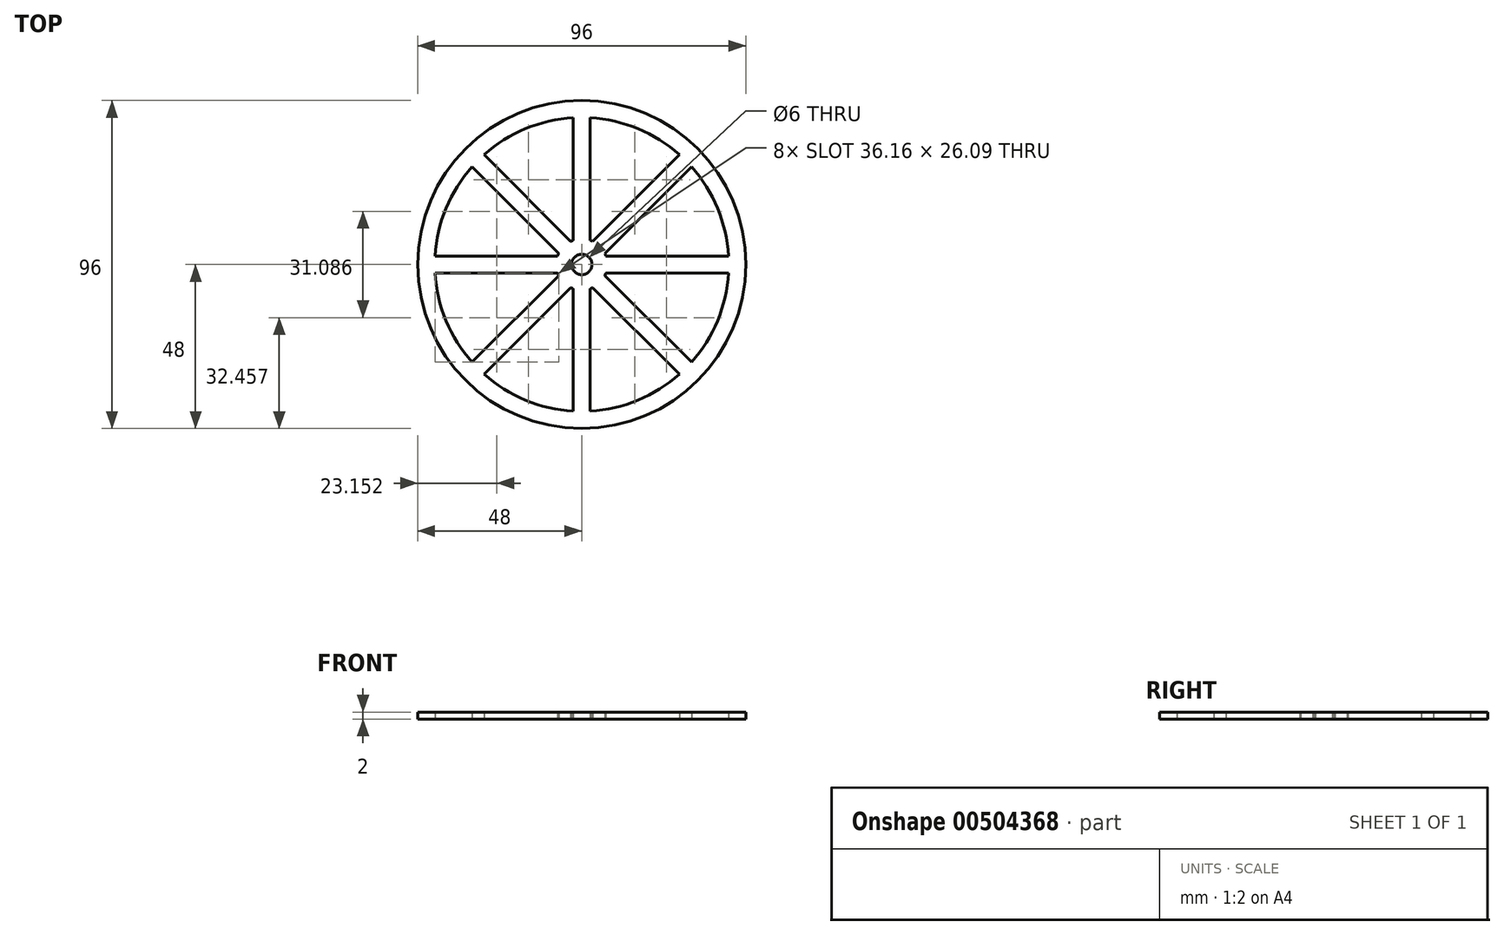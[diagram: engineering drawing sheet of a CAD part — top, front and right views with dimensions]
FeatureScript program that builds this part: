
annotation { "Feature Type Name" : "Feature", "Feature Type Description" : "" }
export const myFeature = defineFeature(function(context is Context, id is Id, definition is map)
    precondition{}
    {
        {
            var Q0;
            Q0=qCreatedBy(makeId("Top.planeOp"),FACE);
            var sketch = newSketch(context, id + "F0", { "sketchPlane" : qUnion([Q0])});
            skArc(sketch, "E0", {"start": v(-32.12, 28.59) * mm, "mid": v(-39.73, 16.46) * mm, "end": v(-42.93, 2.5) * mm});
            skCircle(sketch, "E1", {"center": v(0, 0) * mm, "radius": 48 * mm});
            skLineSegment(sketch, "E2", {"start": v(0, 0) * mm, "end": v(-28.59, 28.59) * mm, "construction": true});
            skLineSegment(sketch, "E3.left", {"start": v(-2.5, 42.93) * mm, "end": v(-2.5, 7.07) * mm});
            skLineSegment(sketch, "E3.right", {"start": v(2.5, 42.93) * mm, "end": v(2.5, 7.07) * mm});
            skLineSegment(sketch, "E4.bottom", {"start": v(-42.93, 2.5) * mm, "end": v(-7.07, 2.5) * mm});
            skLineSegment(sketch, "E4.top", {"start": v(-42.93, -2.5) * mm, "end": v(-7.07, -2.5) * mm});
            skLineSegment(sketch, "E5", {"start": v(-28.59, 32.12) * mm, "end": v(-3.23, 6.77) * mm});
            skLineSegment(sketch, "E6.MirrorCS", {"start": v(-32.12, 28.59) * mm, "end": v(-6.77, 3.23) * mm});
            skLineSegment(sketch, "E7.MirrorCS", {"start": v(28.59, 32.12) * mm, "end": v(3.23, 6.77) * mm});
            skArc(sketch, "E8", {"start": v(-2.5, 7.07) * mm, "mid": v(-2.87, 6.93) * mm, "end": v(-3.23, 6.77) * mm});
            skArc(sketch, "E9.trimOffspring", {"start": v(-6.77, 3.23) * mm, "mid": v(-6.93, 2.87) * mm, "end": v(-7.07, 2.5) * mm});
            skArc(sketch, "E10.trimOffspring", {"start": v(-7.07, -2.5) * mm, "mid": v(-6.93, -2.87) * mm, "end": v(-6.77, -3.23) * mm});
            skLineSegment(sketch, "E11.trimOffspring", {"start": v(-6.77, -3.23) * mm, "end": v(-32.12, -28.59) * mm});
            skArc(sketch, "E12.trimOffspring", {"start": v(-3.23, -6.77) * mm, "mid": v(-2.87, -6.93) * mm, "end": v(-2.5, -7.07) * mm});
            skLineSegment(sketch, "E13.trimOffspring", {"start": v(-3.23, -6.77) * mm, "end": v(-28.59, -32.12) * mm});
            skLineSegment(sketch, "E14.trimOffspring", {"start": v(-2.5, -7.07) * mm, "end": v(-2.5, -42.93) * mm});
            skLineSegment(sketch, "E15.trimOffspring", {"start": v(2.5, -7.07) * mm, "end": v(2.5, -42.93) * mm});
            skLineSegment(sketch, "E16.trimOffspring", {"start": v(3.23, -6.77) * mm, "end": v(28.59, -32.12) * mm});
            skArc(sketch, "E17.trimOffspring", {"start": v(2.5, -7.07) * mm, "mid": v(2.87, -6.93) * mm, "end": v(3.23, -6.77) * mm});
            skArc(sketch, "E18.trimOffspring", {"start": v(6.77, -3.23) * mm, "mid": v(6.93, -2.87) * mm, "end": v(7.07, -2.5) * mm});
            skLineSegment(sketch, "E19.trimOffspring", {"start": v(6.77, -3.23) * mm, "end": v(32.12, -28.59) * mm});
            skLineSegment(sketch, "E20.trimOffspring", {"start": v(7.07, -2.5) * mm, "end": v(42.93, -2.5) * mm});
            skArc(sketch, "E21.trimOffspring", {"start": v(7.07, 2.5) * mm, "mid": v(6.93, 2.87) * mm, "end": v(6.77, 3.23) * mm});
            skArc(sketch, "E22.trimOffspring", {"start": v(3.23, 6.77) * mm, "mid": v(2.87, 6.93) * mm, "end": v(2.5, 7.07) * mm});
            skLineSegment(sketch, "E23.trimOffspring", {"start": v(7.07, 2.5) * mm, "end": v(42.93, 2.5) * mm});
            skPoint(sketch, "E24.MirrorCS.start.orphan", {"position": v(32.12, 28.59) * mm});
            skCircle(sketch, "E25", {"center": v(0, 0) * mm, "radius": 3 * mm});
            skLineSegment(sketch, "E26.MirrorCS", {"start": v(32.12, 28.59) * mm, "end": v(6.77, 3.23) * mm});
            skArc(sketch, "E27.trimOffspring", {"start": v(28.59, 32.12) * mm, "mid": v(0, 43) * mm, "end": v(-28.59, 32.12) * mm});
            skArc(sketch, "E28.trimOffspring", {"start": v(32.12, -28.59) * mm, "mid": v(39.73, -16.46) * mm, "end": v(42.93, -2.5) * mm});
            skArc(sketch, "E29.trimOffspring", {"start": v(-28.59, -32.12) * mm, "mid": v(-16.46, -39.73) * mm, "end": v(-2.5, -42.93) * mm});
            skArc(sketch, "E30.trimOffspring", {"start": v(2.5, -42.93) * mm, "mid": v(16.46, -39.73) * mm, "end": v(28.59, -32.12) * mm});
            skArc(sketch, "E31.trimOffspring", {"start": v(42.93, 2.5) * mm, "mid": v(39.73, 16.46) * mm, "end": v(32.12, 28.59) * mm});
            skArc(sketch, "E32.trimOffspring", {"start": v(-42.93, -2.5) * mm, "mid": v(-39.73, -16.46) * mm, "end": v(-32.12, -28.59) * mm});
            skSolve(sketch);
        }
        {
            var Q0;
            Q0 = qSketchRegion(id + "F0", true);
            extrude(context, id + "F1", {"entities" : qUnion([Q0]), "depth" : 2 * mm});
        }
    });
